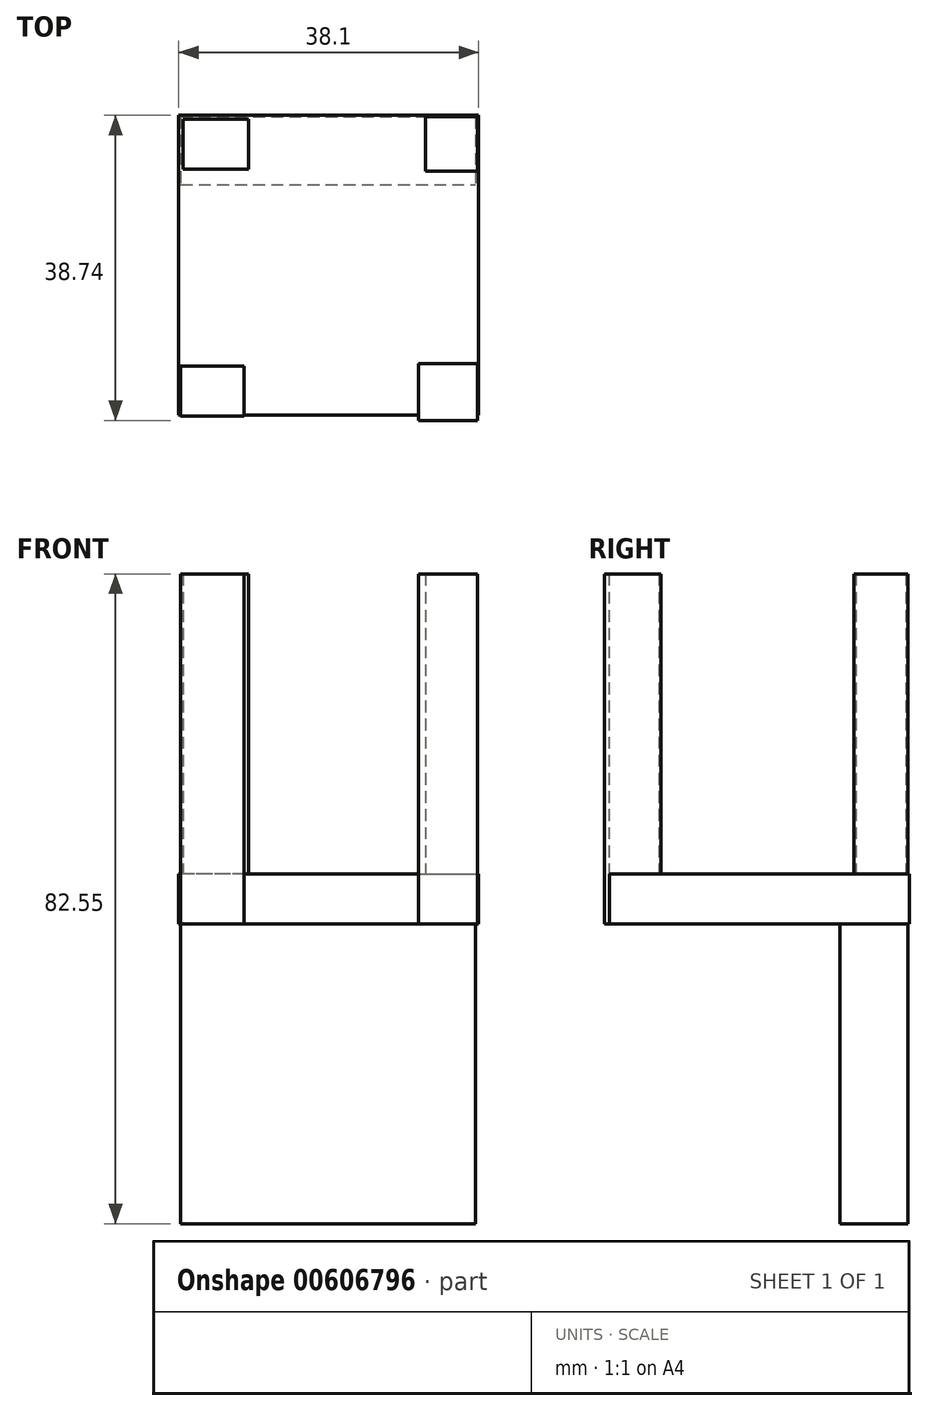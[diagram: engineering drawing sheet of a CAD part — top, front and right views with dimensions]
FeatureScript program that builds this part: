
annotation { "Feature Type Name" : "Feature", "Feature Type Description" : "" }
export const myFeature = defineFeature(function(context is Context, id is Id, definition is map)
    precondition{}
    {
        {
            var Q0;
            Q0=qCreatedBy(makeId("Top.planeOp"),FACE);
            var sketch = newSketch(context, id + "F0", { "sketchPlane" : qUnion([Q0])});
            skLineSegment(sketch, "E0.bottom", {"start": v(-16.82, 19.03) * mm, "end": v(21.28, 19.03) * mm});
            skLineSegment(sketch, "E0.top", {"start": v(-16.82, -19.07) * mm, "end": v(21.28, -19.07) * mm});
            skLineSegment(sketch, "E0.left", {"start": v(-16.82, 19.03) * mm, "end": v(-16.82, -19.07) * mm});
            skLineSegment(sketch, "E0.right", {"start": v(21.28, 19.03) * mm, "end": v(21.28, -19.07) * mm});
            skSolve(sketch);
        }
        {
            var Q0;
            Q0 = qSketchRegion(id + "F0", true);
            extrude(context, id + "F1", {"entities" : qUnion([Q0]), "depth" : 6.35 * mm, "offsetDistance" : 25.4 * mm});
        }
        {
            var Q0;
            Q0=qCreatedBy(makeId("Top.planeOp"),FACE);
            var sketch = newSketch(context, id + "F2", { "sketchPlane" : qUnion([Q0])});
            skLineSegment(sketch, "E1.bottom", {"start": v(-16.55, 18.85) * mm, "end": v(20.87, 18.85) * mm});
            skLineSegment(sketch, "E1.top", {"start": v(-16.55, 10.22) * mm, "end": v(20.87, 10.22) * mm});
            skLineSegment(sketch, "E1.left", {"start": v(-16.55, 18.85) * mm, "end": v(-16.55, 10.22) * mm});
            skLineSegment(sketch, "E1.right", {"start": v(20.87, 18.85) * mm, "end": v(20.87, 10.22) * mm});
            skSolve(sketch);
        }
        {
            var Q0;
            Q0 = qSketchRegion(id + "F2", true);
            extrude(context, id + "F3", {"entities" : qUnion([Q0]), "operationType" : NewBodyOperationType.ADD, "oppositeDirection" : true, "depth" : 38.1 * mm, "offsetDistance" : 25.4 * mm});
        }
        {
            var Q0;
            Q0=qCreatedBy(makeId("Top.planeOp"),FACE);
            var sketch = newSketch(context, id + "F4", { "sketchPlane" : qUnion([Q0])});
            skLineSegment(sketch, "E2.bottom", {"start": v(-16.55, -19.14) * mm, "end": v(-8.5, -19.14) * mm});
            skLineSegment(sketch, "E2.top", {"start": v(-16.55, -12.8) * mm, "end": v(-8.5, -12.8) * mm});
            skLineSegment(sketch, "E2.left", {"start": v(-16.55, -19.14) * mm, "end": v(-16.55, -12.8) * mm});
            skLineSegment(sketch, "E2.right", {"start": v(-8.5, -19.14) * mm, "end": v(-8.5, -12.8) * mm});
            skLineSegment(sketch, "E3.bottom", {"start": v(21.15, -19.71) * mm, "end": v(13.67, -19.71) * mm});
            skLineSegment(sketch, "E3.top", {"start": v(21.15, -12.52) * mm, "end": v(13.67, -12.52) * mm});
            skLineSegment(sketch, "E3.left", {"start": v(21.15, -19.71) * mm, "end": v(21.15, -12.52) * mm});
            skLineSegment(sketch, "E3.right", {"start": v(13.67, -19.71) * mm, "end": v(13.67, -12.52) * mm});
            skLineSegment(sketch, "E4.bottom", {"start": v(-16.26, 18.56) * mm, "end": v(-7.91, 18.56) * mm});
            skLineSegment(sketch, "E4.top", {"start": v(-16.26, 12.23) * mm, "end": v(-7.91, 12.23) * mm});
            skLineSegment(sketch, "E4.left", {"start": v(-16.26, 18.56) * mm, "end": v(-16.26, 12.23) * mm});
            skLineSegment(sketch, "E4.right", {"start": v(-7.91, 18.56) * mm, "end": v(-7.91, 12.23) * mm});
            skLineSegment(sketch, "E5.bottom", {"start": v(21.15, 18.85) * mm, "end": v(14.53, 18.85) * mm});
            skLineSegment(sketch, "E5.top", {"start": v(21.15, 11.94) * mm, "end": v(14.53, 11.94) * mm});
            skLineSegment(sketch, "E5.left", {"start": v(21.15, 18.85) * mm, "end": v(21.15, 11.94) * mm});
            skLineSegment(sketch, "E5.right", {"start": v(14.53, 18.85) * mm, "end": v(14.53, 11.94) * mm});
            skSolve(sketch);
        }
        {
            var Q0;
            Q0 = qSketchRegion(id + "F4", true);
            extrude(context, id + "F5", {"entities" : qUnion([Q0]), "operationType" : NewBodyOperationType.ADD, "depth" : 44.45 * mm, "offsetDistance" : 25.4 * mm});
        }
    });
